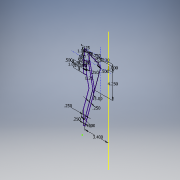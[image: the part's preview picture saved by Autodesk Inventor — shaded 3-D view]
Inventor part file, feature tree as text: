
AUTODESK INVENTOR PART (.ipt)
format: ipt  version: 2017 SP1 (Build 210196100, 196)  size: 128,000 bytes
history: native  units: in
note: dims shown in document units (in); Inventor stores cm internally (conversion verified against a paired STEP export)
features: sketch x1
ambient origin geometry x8: Origin, YZ Plane, XZ Plane, XY Plane, X Axis, Y Axis, Z Axis, Center Point
feature tree (1):
  sketch  "Sketch1"  dims[d0=1.13in d3=0.1718in d5=1.0in d6=1.0in d7=90.0deg d8=0.5in d9=15.0deg d31=0.25in d34=15.0deg d37=1.75in d40=3.75in d41=0.125in d46=0.75in d47=0.5in d50=3.4in d51=0.5in d52=0.25in d53=0.5in d54=0.5in d55=0.5in d56=1.25in d58=0.0017in d59=0.5in d60=0.5in d61=1.0in d62=0.234in d63=0.234in d64=0.125in d65=0.25in d67=0.25in d68=4.25in d69=0.25in d70=0.25in]
